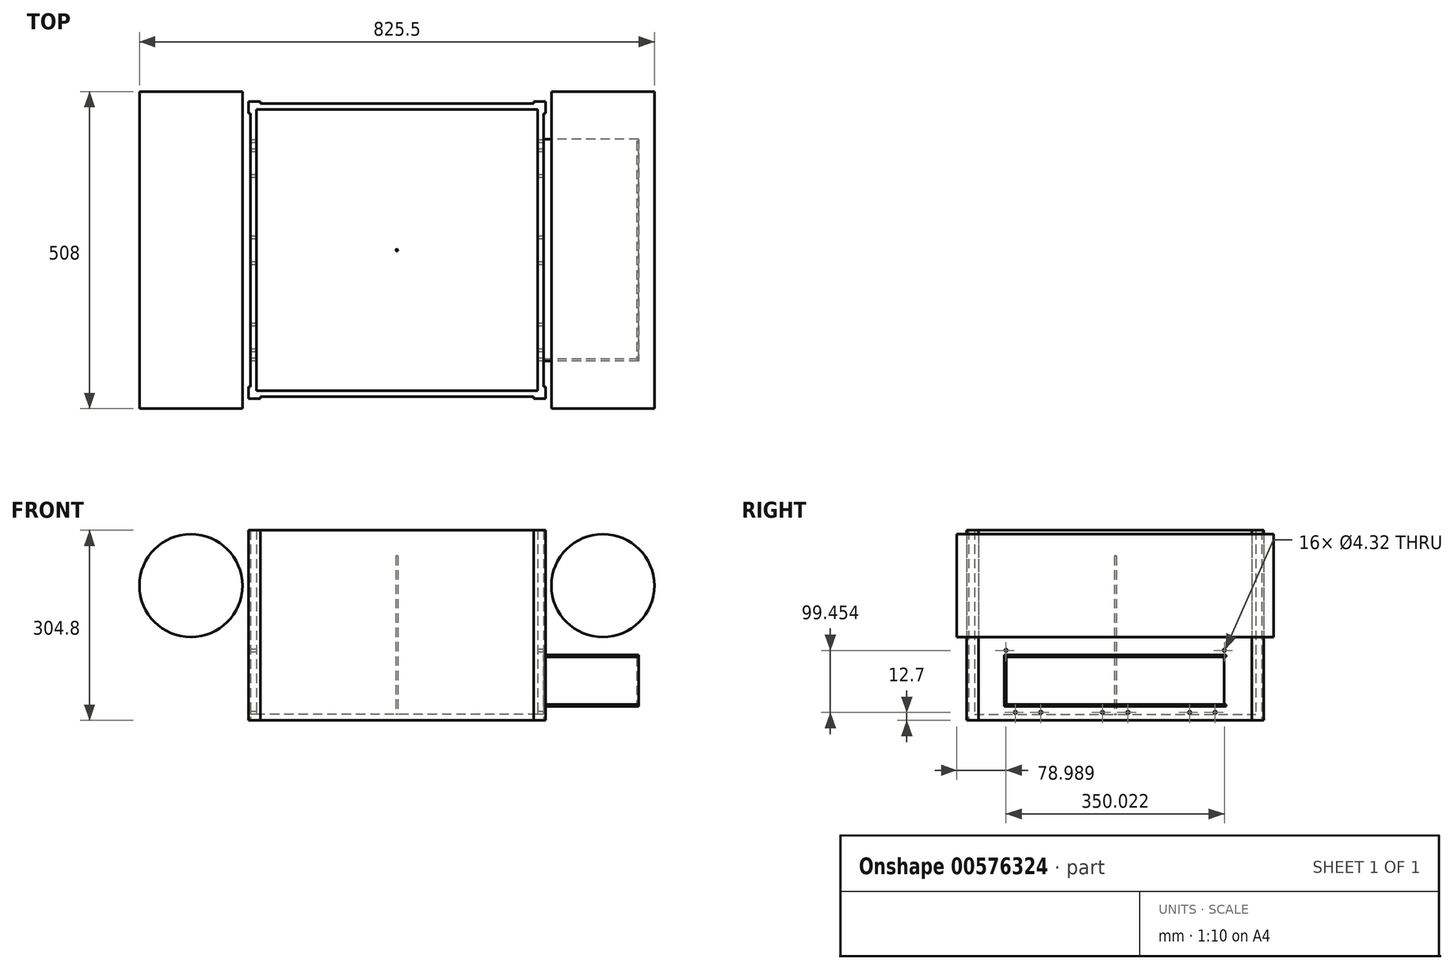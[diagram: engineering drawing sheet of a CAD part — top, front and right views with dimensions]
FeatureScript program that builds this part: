
annotation { "Feature Type Name" : "Feature", "Feature Type Description" : "" }
export const myFeature = defineFeature(function(context is Context, id is Id, definition is map)
    precondition{}
    {
        {
            var Q0;
            Q0=qCreatedBy(makeId("Top.planeOp"),FACE);
            var sketch = newSketch(context, id + "F0", { "sketchPlane" : qUnion([Q0])});
            skLineSegment(sketch, "E0.bottom", {"start": v(234.95, -234.95) * mm, "end": v(-234.95, -234.95) * mm});
            skLineSegment(sketch, "E0.top", {"start": v(234.95, 234.95) * mm, "end": v(-234.95, 234.95) * mm});
            skLineSegment(sketch, "E0.left", {"start": v(234.95, -234.95) * mm, "end": v(234.95, 234.95) * mm});
            skLineSegment(sketch, "E0.right", {"start": v(-234.95, -234.95) * mm, "end": v(-234.95, 234.95) * mm});
            skPoint(sketch, "E0.middle", {"position": v(0, 0) * mm});
            skLineSegment(sketch, "E1", {"start": v(-234.95, 234.95) * mm, "end": v(-234.95, 238.13) * mm});
            skLineSegment(sketch, "E2", {"start": v(-234.95, 238.13) * mm, "end": v(-238.13, 238.13) * mm});
            skLineSegment(sketch, "E3", {"start": v(-238.13, 238.13) * mm, "end": v(-238.13, 219.08) * mm});
            skLineSegment(sketch, "E4", {"start": v(-238.13, 238.13) * mm, "end": v(-219.08, 238.13) * mm});
            skLineSegment(sketch, "E5", {"start": v(-219.08, 238.13) * mm, "end": v(-219.08, 234.95) * mm});
            skLineSegment(sketch, "E6", {"start": v(-238.13, 219.08) * mm, "end": v(-234.95, 219.08) * mm});
            skLineSegment(sketch, "E7.1.0", {"start": v(-238.13, -234.95) * mm, "end": v(-238.13, -238.12) * mm});
            skLineSegment(sketch, "E7.1.1", {"start": v(-238.13, -219.07) * mm, "end": v(-234.95, -219.07) * mm});
            skLineSegment(sketch, "E7.1.2", {"start": v(-238.13, -238.12) * mm, "end": v(-219.08, -238.12) * mm});
            skLineSegment(sketch, "E7.1.3", {"start": v(-234.95, -234.95) * mm, "end": v(-238.13, -234.95) * mm});
            skLineSegment(sketch, "E7.1.4", {"start": v(-238.13, -238.12) * mm, "end": v(-238.13, -219.07) * mm});
            skLineSegment(sketch, "E7.1.5", {"start": v(-219.08, -238.13) * mm, "end": v(-219.08, -234.95) * mm});
            skLineSegment(sketch, "E7.2.0", {"start": v(234.95, -238.13) * mm, "end": v(238.12, -238.13) * mm});
            skLineSegment(sketch, "E7.2.1", {"start": v(219.07, -238.13) * mm, "end": v(219.07, -234.95) * mm});
            skLineSegment(sketch, "E7.2.2", {"start": v(238.12, -238.13) * mm, "end": v(238.12, -219.08) * mm});
            skLineSegment(sketch, "E7.2.3", {"start": v(234.95, -234.95) * mm, "end": v(234.95, -238.13) * mm});
            skLineSegment(sketch, "E7.2.4", {"start": v(238.12, -238.13) * mm, "end": v(219.07, -238.13) * mm});
            skLineSegment(sketch, "E7.2.5", {"start": v(238.12, -219.08) * mm, "end": v(234.95, -219.08) * mm});
            skLineSegment(sketch, "E7.3.0", {"start": v(238.13, 234.95) * mm, "end": v(238.13, 238.12) * mm});
            skLineSegment(sketch, "E7.3.1", {"start": v(238.13, 219.07) * mm, "end": v(234.95, 219.07) * mm});
            skLineSegment(sketch, "E7.3.2", {"start": v(238.13, 238.12) * mm, "end": v(219.08, 238.12) * mm});
            skLineSegment(sketch, "E7.3.3", {"start": v(234.95, 234.95) * mm, "end": v(238.13, 234.95) * mm});
            skLineSegment(sketch, "E7.3.4", {"start": v(238.13, 238.12) * mm, "end": v(238.13, 219.07) * mm});
            skLineSegment(sketch, "E7.3.5", {"start": v(219.08, 238.12) * mm, "end": v(219.08, 234.95) * mm});
            skLineSegment(sketch, "E8.0", {"start": v(225.43, 225.43) * mm, "end": v(-225.43, 225.43) * mm});
            skLineSegment(sketch, "E8.1", {"start": v(225.42, -225.42) * mm, "end": v(225.43, 225.43) * mm});
            skLineSegment(sketch, "E8.2", {"start": v(225.42, -225.42) * mm, "end": v(-225.43, -225.43) * mm});
            skLineSegment(sketch, "E8.3", {"start": v(-225.43, -225.42) * mm, "end": v(-225.43, 225.42) * mm});
            skSolve(sketch);
        }
        {
            var Q0;
            Q0=qSketchRegion(id+"F0",true);
            extrude(context, id + "F1", {"entities" : qUnion([Q0]), "depth" : 304.8 * mm, "offsetDistance" : 25.4 * mm});
        }
        {
            var Q0;
            Q0=makeQuery(id+"F0.imprint","IMPRINT",FACE,{"disambiguationData":[TD([[makeQuery(id+"F0.imprint","IMPRINT",EDGE,{"derivedFrom":sQuery(id+"F0.wireOp",EDGE,"E8.0")}),1.0]])]});
            extrude(context, id + "F2", {"entities" : qUnion([Q0]), "operationType" : NewBodyOperationType.ADD, "depth" : 9.52 * mm, "offsetDistance" : 25.4 * mm});
        }
        {
            var Q0;
            Q0=qCreatedBy(makeId("Front.planeOp"),FACE);
            var sketch = newSketch(context, id + "F3", { "sketchPlane" : qUnion([Q0])});
            skLineSegment(sketch, "E9", {"start": v(0, 0) * mm, "end": v(234.95, 0) * mm});
            skLineSegment(sketch, "E10", {"start": v(234.95, 0) * mm, "end": v(234.95, 215.9) * mm});
            skLineSegment(sketch, "E11", {"start": v(234.95, 215.9) * mm, "end": v(330.2, 215.9) * mm});
            skCircle(sketch, "E12", {"center": v(330.2, 215.9) * mm, "radius": 82.55 * mm});
            skSolve(sketch);
        }
        {
            var Q0;
            Q0=qSketchRegion(id+"F3",true);
            extrude(context, id + "F4", {"entities" : qUnion([Q0]), "endBound" : BoundingType.SYMMETRIC, "depth" : 508 * mm, "offsetDistance" : 25.4 * mm});
        }
        {
            var Q0;
            Q0=makeQuery(id+"F4.opExtrude","SWEPT_BODY",BODY,{"disambiguationData":[OSD([sQuery(id+"F3.wireOp",EDGE,"E12")])]});
            var Q1;
            Q1=qCreatedBy(makeId("Right.planeOp"),FACE);
            mirror(context, id + "F5", {"entities" : qUnion([Q0]), "mirrorPlane" : qUnion([Q1])});
        }
        {
            var Q0;
            Q0=makeQuery(id+"F1.opExtrude","SWEPT_FACE",FACE,{"disambiguationData":[OSD([sQuery(id+"F0.wireOp",EDGE,"E0.left")])]});
            var sketch = newSketch(context, id + "F6", { "sketchPlane" : qUnion([Q0])});
            skLineSegment(sketch, "E13", {"start": v(0, 0) * mm, "end": v(0, 12.7) * mm});
            skLineSegment(sketch, "E14", {"start": v(0, 12.7) * mm, "end": v(0, 112.15) * mm});
            skLineSegment(sketch, "E15", {"start": v(0, 112.15) * mm, "end": v(175.01, 112.15) * mm});
            skLineSegment(sketch, "E16", {"start": v(0, 12.7) * mm, "end": v(139.7, 12.7) * mm});
            skLineSegment(sketch, "E17", {"start": v(69.85, 12.7) * mm, "end": v(139.7, 12.7) * mm});
            skLineSegment(sketch, "E18", {"start": v(0, 12.7) * mm, "end": v(-20.52, 12.7) * mm});
            skLineSegment(sketch, "E19.MirrorCS", {"start": v(-69.85, 12.7) * mm, "end": v(-139.7, 12.7) * mm});
            skLineSegment(sketch, "E20.MirrorCS", {"start": v(0, 12.7) * mm, "end": v(20.52, 12.7) * mm});
            skLineSegment(sketch, "E21.MirrorCS", {"start": v(0, 12.7) * mm, "end": v(-139.7, 12.7) * mm});
            skLineSegment(sketch, "E22.MirrorCS", {"start": v(0, 112.15) * mm, "end": v(-175.01, 112.15) * mm});
            skLineSegment(sketch, "E23", {"start": v(69.85, 12.7) * mm, "end": v(69.85, 28.2) * mm});
            skLineSegment(sketch, "E24.MirrorCS", {"start": v(139.7, 12.7) * mm, "end": v(119.18, 12.7) * mm});
            skLineSegment(sketch, "E25.MirrorCS", {"start": v(139.7, 12.7) * mm, "end": v(160.22, 12.7) * mm});
            skLineSegment(sketch, "E26.MirrorCS", {"start": v(-139.7, 12.7) * mm, "end": v(-119.18, 12.7) * mm});
            skLineSegment(sketch, "E27.MirrorCS", {"start": v(-139.7, 12.7) * mm, "end": v(-160.22, 12.7) * mm});
            skSolve(sketch);
        }
        {
            var Q0;
            Q0=sQuery(id+"F6.wireOp",VERTEX,"E22.MirrorCS.end");
            var Q1;
            Q1=sQuery(id+"F6.wireOp",VERTEX,"E15.end");
            var Q2;
            Q2=sQuery(id+"F6.wireOp",VERTEX,"E25.MirrorCS.end");
            var Q3;
            Q3=sQuery(id+"F6.wireOp",VERTEX,"E24.MirrorCS.end");
            var Q4;
            Q4=sQuery(id+"F6.wireOp",VERTEX,"E20.MirrorCS.end");
            var Q5;
            Q5=sQuery(id+"F6.wireOp",VERTEX,"E26.MirrorCS.end");
            var Q6;
            Q6=sQuery(id+"F6.wireOp",VERTEX,"E27.MirrorCS.end");
            var Q7;
            Q7=sQuery(id+"F6.wireOp",VERTEX,"E18.end");
            var Q8;
            Q8=makeQuery(id+"F1.opExtrude","SWEPT_BODY",BODY,{"disambiguationData":[OSD([sQuery(id+"F0.wireOp",EDGE,"E0.bottom"),sQuery(id+"F0.wireOp",EDGE,"E0.top"),sQuery(id+"F0.wireOp",EDGE,"E0.left"),sQuery(id+"F0.wireOp",EDGE,"E0.right"),sQuery(id+"F0.wireOp",EDGE,"E3"),sQuery(id+"F0.wireOp",EDGE,"E4"),sQuery(id+"F0.wireOp",EDGE,"E5"),sQuery(id+"F0.wireOp",EDGE,"E6"),sQuery(id+"F0.wireOp",EDGE,"E7.1.1"),sQuery(id+"F0.wireOp",EDGE,"E7.1.2"),sQuery(id+"F0.wireOp",EDGE,"E7.1.4"),sQuery(id+"F0.wireOp",EDGE,"E7.1.5"),sQuery(id+"F0.wireOp",EDGE,"E7.2.1"),sQuery(id+"F0.wireOp",EDGE,"E7.2.2"),sQuery(id+"F0.wireOp",EDGE,"E7.2.4"),sQuery(id+"F0.wireOp",EDGE,"E7.2.5"),sQuery(id+"F0.wireOp",EDGE,"E7.3.1"),sQuery(id+"F0.wireOp",EDGE,"E7.3.2"),sQuery(id+"F0.wireOp",EDGE,"E7.3.4"),sQuery(id+"F0.wireOp",EDGE,"E7.3.5"),sQuery(id+"F0.wireOp",EDGE,"E8.0"),sQuery(id+"F0.wireOp",EDGE,"E8.1"),sQuery(id+"F0.wireOp",EDGE,"E8.2"),sQuery(id+"F0.wireOp",EDGE,"E8.3")])]});
            hole(context, id + "F7", {"style" : HoleStyle.SIMPLE, "endStyle" : HoleEndStyle.BLIND, "standardTappedOrClearance" : lookupTablePath({ "standard" : "ANSI", "fit" : "Close", "size" : "#8", "type" : "Clearance" }), "standardBlindInLast" : lookupTablePath({ "fit" : "Close", "standard" : "ANSI", "size" : "#8", "type" : "Clearance" }), "holeDiameter" : 4.32 * mm, "holeDepth" : 762 * mm, "isTappedThrough" : true, "tappedDepth" : 12.7 * mm, "tapClearance" : 3, "locations" : qUnion([Q0, Q1, Q2, Q3, Q4, Q5, Q6, Q7]), "scope" : qUnion([Q8])});
        }
        {
            var Q0;
            Q0=makeQuery(id+"F1.opExtrude","SWEPT_FACE",FACE,{"disambiguationData":[OSD([sQuery(id+"F0.wireOp",EDGE,"E0.left")])]});
            var sketch = newSketch(context, id + "F8", { "sketchPlane" : qUnion([Q0])});
            skLineSegment(sketch, "E28", {"start": v(0, 0) * mm, "end": v(0, 22.22) * mm});
            skPoint(sketch, "E28.endSnap0", {"position": v(0, 0) * mm});
            skLineSegment(sketch, "E29", {"start": v(0, 22.22) * mm, "end": v(-177.8, 22.22) * mm});
            skLineSegment(sketch, "E30", {"start": v(-177.8, 22.22) * mm, "end": v(-177.8, 104.77) * mm});
            skLineSegment(sketch, "E31", {"start": v(-177.8, 104.77) * mm, "end": v(0, 104.77) * mm});
            skLineSegment(sketch, "E32.MirrorCS", {"start": v(177.8, 22.22) * mm, "end": v(177.8, 104.77) * mm});
            skLineSegment(sketch, "E33.MirrorCS", {"start": v(0, 22.22) * mm, "end": v(177.8, 22.23) * mm});
            skLineSegment(sketch, "E34.MirrorCS", {"start": v(177.8, 104.77) * mm, "end": v(0, 104.77) * mm});
            skLineSegment(sketch, "E35", {"start": v(-177.8, 104.77) * mm, "end": v(-177.8, 101.6) * mm});
            skLineSegment(sketch, "E36", {"start": v(-177.8, 101.6) * mm, "end": v(177.8, 101.6) * mm});
            skLineSegment(sketch, "E37", {"start": v(177.8, 101.6) * mm, "end": v(174.62, 101.6) * mm});
            skLineSegment(sketch, "E38", {"start": v(174.63, 63.5) * mm, "end": v(160.14, 63.5) * mm});
            skLineSegment(sketch, "E39.MirrorCS", {"start": v(-177.8, 25.4) * mm, "end": v(177.8, 25.4) * mm});
            skLineSegment(sketch, "E40", {"start": v(174.62, 101.6) * mm, "end": v(174.62, 25.4) * mm});
            skLineSegment(sketch, "E41.MirrorCS", {"start": v(-174.63, 101.6) * mm, "end": v(-174.63, 25.4) * mm});
            skPoint(sketch, "E42.orphan", {"position": v(177.8, 63.5) * mm});
            skSolve(sketch);
        }
        {
            var Q0;
            {var subQ6=sQuery(id+"F8.wireOp",EDGE,"E29");Q0=makeQuery(id+"F8.imprint","IMPRINT",FACE,{"disambiguationData":[TD([[makeQuery(id+"F8.imprint","IMPRINT",EDGE,{"derivedFrom":subQ6}),-1.0]])]});}
            var Q1;
            Q1=makeQuery(id+"F8.imprint","IMPRINT",FACE,{"disambiguationData":[TD([[makeQuery(id+"F8.imprint","IMPRINT",EDGE,{"derivedFrom":sQuery(id+"F8.wireOp",EDGE,"E31")}),-1.0]])]});
            extrude(context, id + "F9", {"entities" : qUnion([Q0, Q1]), "depth" : 152.4 * mm, "offsetDistance" : 25.4 * mm});
        }
        {
            var Q0;
            {var subQ5=sQuery(id+"F8.wireOp",EDGE,"E41.MirrorCS");Q0=makeQuery(id+"F8.imprint","IMPRINT",FACE,{"disambiguationData":[TD([[makeQuery(id+"F8.imprint","IMPRINT",EDGE,{"derivedFrom":subQ5}),-1.0]])]});}
            var Q1;
            {var subQ1=sQuery(id+"F8.wireOp",EDGE,"E37");Q1=makeQuery(id+"F8.imprint","IMPRINT",FACE,{"disambiguationData":[TD([[makeQuery(id+"F8.imprint","IMPRINT",EDGE,{"derivedFrom":subQ1}),1.0]])]});}
            extrude(context, id + "F10", {"entities" : qUnion([Q0, Q1]), "depth" : 152.4 * mm, "offsetDistance" : 25.4 * mm});
        }
        {
            var Q0;
            Q0=makeQuery(id+"F9.opExtrude","SWEPT_FACE",FACE,{"disambiguationData":[OSD([sQuery(id+"F8.wireOp",EDGE,"E39.MirrorCS")])]});
            var sketch = newSketch(context, id + "F11", { "sketchPlane" : qUnion([Q0])});
            skLineSegment(sketch, "E43", {"start": v(387.35, 174.62) * mm, "end": v(384.18, 174.62) * mm});
            skLineSegment(sketch, "E44", {"start": v(384.18, 174.62) * mm, "end": v(384.18, -174.63) * mm});
            skLineSegment(sketch, "E45", {"start": v(384.18, -174.63) * mm, "end": v(387.35, -174.63) * mm});
            skLineSegment(sketch, "E46", {"start": v(387.35, -174.63) * mm, "end": v(387.35, 174.62) * mm});
            skSolve(sketch);
        }
        {
            var Q0;
            Q0=qSketchRegion(id+"F11",true);
            var Q1;
            Q1=makeQuery(id+"F9.opExtrude","SWEPT_FACE",FACE,{"disambiguationData":[OSD([sQuery(id+"F8.wireOp",EDGE,"E36"),sQuery(id+"F8.wireOp",EDGE,"E37")])]});
            extrude(context, id + "F12", {"entities" : qUnion([Q0]), "endBound" : BoundingType.UP_TO_SURFACE, "depth" : 25.4 * mm, "endBoundEntityFace" : qUnion([Q1]), "offsetDistance" : 25.4 * mm});
        }
        {
            var Q0;
            Q0=makeQuery(id+"F2.opExtrude","CAP_FACE",FACE,{"disambiguationData":[OSD([sQuery(id+"F0.wireOp",EDGE,"E8.0"),sQuery(id+"F0.wireOp",EDGE,"E8.1"),sQuery(id+"F0.wireOp",EDGE,"E8.2"),sQuery(id+"F0.wireOp",EDGE,"E8.3")])],"isStart":false});
            var sketch = newSketch(context, id + "F13", { "sketchPlane" : qUnion([Q0])});
            skCircle(sketch, "E47", {"center": v(0, 0) * mm, "radius": 1.59 * mm});
            skSolve(sketch);
        }
        {
            var Q0;
            Q0=qSketchRegion(id+"F13",true);
            extrude(context, id + "F14", {"entities" : qUnion([Q0]), "operationType" : NewBodyOperationType.ADD, "depth" : 254 * mm, "offsetDistance" : 25.4 * mm});
        }
    });
